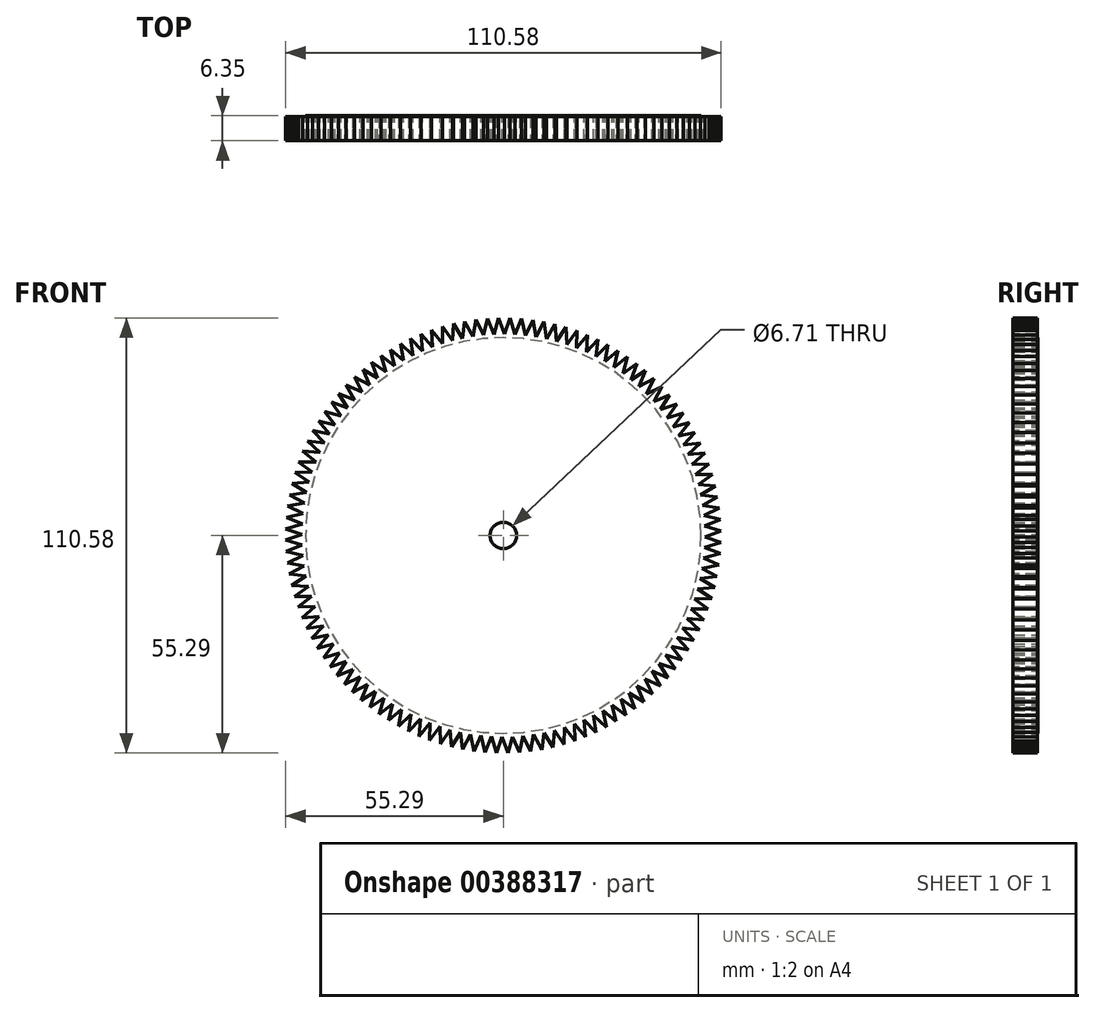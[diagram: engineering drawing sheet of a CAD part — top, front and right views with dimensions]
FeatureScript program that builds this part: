
annotation { "Feature Type Name" : "Feature", "Feature Type Description" : "" }
export const myFeature = defineFeature(function(context is Context, id is Id, definition is map)
    precondition{}
    {
        {
            var Q0;
            Q0=qCreatedBy(makeId("Front.planeOp"),FACE);
            var sketch = newSketch(context, id + "F0", { "sketchPlane" : qUnion([Q0])});
            skCircle(sketch, "E0", {"center": v(0, 0) * mm, "radius": 50.25 * mm});
            skCircle(sketch, "E1", {"center": v(0, 0) * mm, "radius": 3.35 * mm});
            skSolve(sketch);
        }
        {
            var Q0;
            Q0=qSketchRegion(id+"F0",true);
            extrude(context, id + "F1", {"entities" : qUnion([Q0]), "depth" : 6.35 * mm});
        }
        {
            var Q0;
            Q0=makeQuery(id+"F1.opExtrude","CAP_FACE",FACE,{"disambiguationData":[OSD([sQuery(id+"F0.wireOp",EDGE,"E0"),sQuery(id+"F0.wireOp",EDGE,"E1")])],"isStart":false});
            var sketch = newSketch(context, id + "F2", { "sketchPlane" : qUnion([Q0])});
            skLineSegment(sketch, "E2", {"start": v(0, 50.25) * mm, "end": v(1.72, 55.28) * mm});
            skLineSegment(sketch, "E3", {"start": v(1.72, 55.28) * mm, "end": v(3.27, 50.14) * mm});
            skSolve(sketch);
        }
        {
            var Q0;
            Q0=qCreatedBy(makeId("Right.planeOp"),FACE);
            var sketch = newSketch(context, id + "F3", { "sketchPlane" : qUnion([Q0])});
            skLineSegment(sketch, "E4", {"start": v(0, 0) * mm, "end": v(-34.15, 0) * mm});
            skSolve(sketch);
        }
        {
            var Q0;
            {var subQ0=sQuery(id+"F2.wireOp",EDGE,"E2");Q0=makeQuery(id+"F2.imprint","IMPRINT",FACE,{"disambiguationData":[TD([[makeQuery(id+"F2.imprint","IMPRINT",EDGE,{"derivedFrom":subQ0}),-1.0]])]});}
            extrude(context, id + "F4", {"entities" : qUnion([Q0]), "oppositeDirection" : true, "depth" : 6.2 * mm});
        }
        {
            var Q0;
            Q0=makeQuery(id+"F4.opExtrude","SWEPT_BODY",BODY,{"disambiguationData":[OSD([sQuery(id+"F0.wireOp",EDGE,"E0"),sQuery(id+"F2.wireOp",EDGE,"E2"),sQuery(id+"F2.wireOp",EDGE,"E3")])]});
            var Q1;
            Q1=sQuery(id+"F3.wireOp",EDGE,"E4");
            circularPattern(context, id + "F5", {"operationType" : NewBodyOperationType.ADD, "entities" : qUnion([Q0]), "axis" : qUnion([Q1]), "angle" : 360 * degree, "instanceCount" : 120, "equalSpace" : true});
        }
    });
